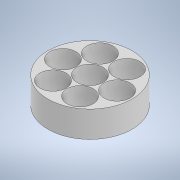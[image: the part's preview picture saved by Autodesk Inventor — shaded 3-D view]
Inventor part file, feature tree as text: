
AUTODESK INVENTOR PART (.ipt)
format: ipt  version: 2022 (Build 260153000, 153)  size: 139,776 bytes
history: native  units: mm
features: extrude x1, sketch x1
ambient origin geometry x8: Origin, YZ Plane, XZ Plane, XY Plane, X Axis, Y Axis, Z Axis, Center Point
bodies: Solid1 (feature_tree)
feature tree (2):
  extrude  "Extrusion1"  Depth=30.0mm
  sketch  "Sketch1"  dims[d0=32.0mm d1=30.0mm d2=60.0mm d4=360.0deg d6=32.0mm d7=30.0mm d8=0.0mm d19=30.0mm d20=0.872665mm d21=0.5mm d22=0.872665mm]
